# Revit family: Haworth_BuzziJet_Pendant_Lighting_AP_PRELIMINARY
name_source: partatom
category: Lighting Fixtures
revit_build: Autodesk Revit 2018 (Build: 20170223_1515(x64)
units: mm (PartAtom-declared; Revit-internal decimal feet)

## family parameters
Cut with Voids When Loaded = No
Host = Face
Light Source = No
Part Type = Normal
Room Calculation Point = No
Round Connector Dimension = Use Diameter
Shared = No

## types (4) — shared parameters
Actual Depth = 800 mm  [stored 2.62467 ft]
Actual Width = 800 mm  [stored 2.62467 ft]
Assembly Code = E2020200
Description = Haworth - BuzziJet - Pendant - Lighting
Glass Finish = Haworth _ Glass _ Frosted
Manufacturer = Haworth
Max. Cable Length = 5000 mm  [stored 16.4042 ft]
Min. Cable Length = 508 mm
Model = Buzzi Jet
Note = Verify Final Dim. w/ Haworth
Revision = 1
Split Cable Length = 400 mm  [stored 1.31234 ft]
Trim Finish = Haworth _ Paint _ Collection Black
URL = https://www.haworth.com
URL - Product = https://www.haworth.com
Warranty = http://www.haworth.com
zero-valued in all types: Default Elevation

## per-type parameters (varying)
| type | Actual Height | Medium | Small | Split Cable | Straight Cable |
| Medium Pendant - Split Cable | 450 mm  [stored 1.47638 ft] | Yes | No | Yes | No |
| Medium Pendant - Straight Cable | 450 mm  [stored 1.47638 ft] | Yes | No | No | Yes |
| Small Pendant - Split Cable | 225 mm  [stored 0.738189 ft] | No | Yes | Yes | No |
| Small Pendant - Straight Cable | 225 mm  [stored 0.738189 ft] | No | Yes | No | Yes |

note: [stored X ft] marks values corroborated as IEEE doubles in the binary element streams (Revit-internal decimal feet)

## geometry (parser evidence)
native form markers: Sweep x6
no freeform markers — native parametric forms only
